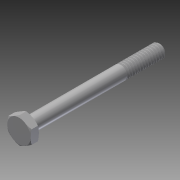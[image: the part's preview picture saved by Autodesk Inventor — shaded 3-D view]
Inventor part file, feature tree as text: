
AUTODESK INVENTOR PART (.ipt)
format: ipt  version: 2014 SP1 (Build 180222100, 222)  size: 495,616 bytes
history: native  units: in
note: dims shown in document units (in); Inventor stores cm internally (conversion verified against a paired STEP export)
features: extrude x1, other x1, imported_body x1
ambient origin geometry x8: Origin, YZ Plane, XZ Plane, XY Plane, X Axis, Y Axis, Z Axis, Center Point
bodies: Body1 (feature_tree)
feature tree (3):
  extrude  "Extrude14"  [1 undecoded]
  other  "91257A5521"
  imported_body  "Base1"
note: 1 required parameter value undecoded (feature->parameter linkage not recoverable at this tier; creation-order binding heuristic only, values carry confidence <= 0.55)
